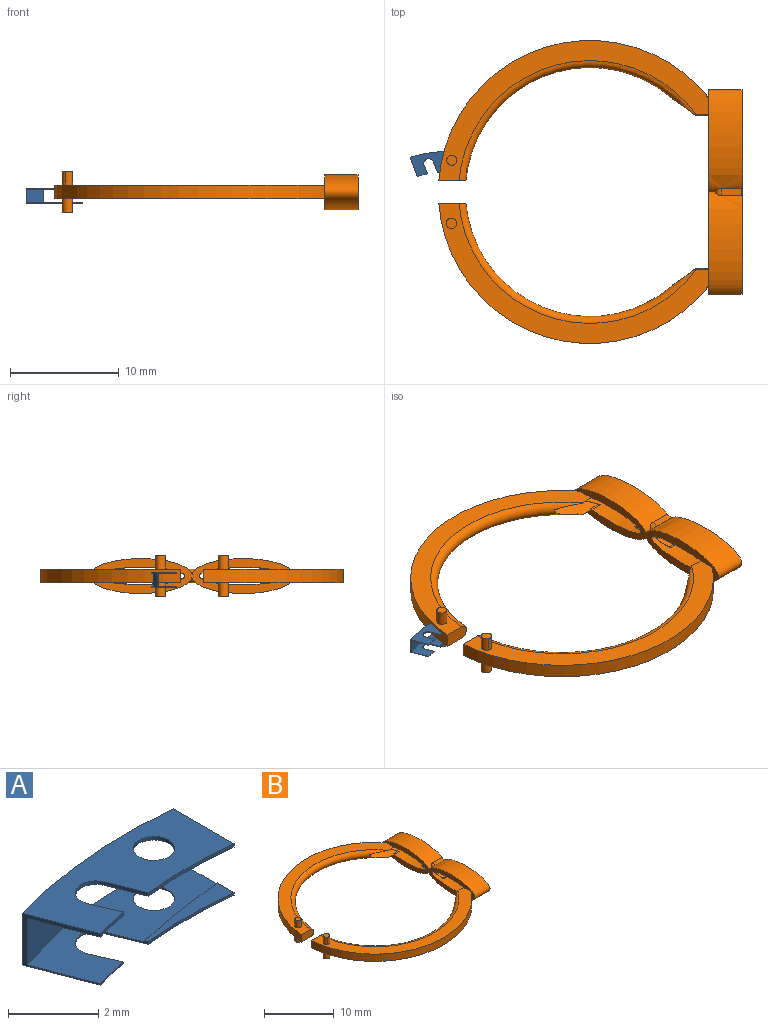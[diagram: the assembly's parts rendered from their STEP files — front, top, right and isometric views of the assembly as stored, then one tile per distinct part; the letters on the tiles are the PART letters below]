
ASSEMBLY  parts=2 mates=1
PART A: 27 faces, bbox 5.2x2.3x1.4 mm
  f0: cylinder r=12.03mm len=0.96mm, axis (0,0,-1), area 0.1mm2, adj f1,f4,f20,f26
  f1: plane 5.2x2.31mm, normal (0,0,1), area 7.4mm2, adj f0,f6,f12,f13,f16,f20,f21,f22
  f2: plane 5.2x2.31mm, normal (0,0,-1), area 7.4mm2, adj f5,f6,f8,f14,f15,f23,f24,f25
  f3: plane 5.15x2.31mm, normal (0,0,1), area 6.5mm2, adj f5,f6,f7,f9,f14,f15,f23,f24
  f4: plane 5.16x2.34mm, normal (0,0,-1), area 6.5mm2, adj f0,f6,f7,f11,f13,f16,f19,f20
  f5: cylinder r=12.03mm len=0.96mm, axis (0,0,-1), area 0mm2, adj f2,f3,f25,f26
  f6: cylinder r=13.92mm len=5.2mm, axis (0,0,-1), area 2.8mm2, adj f1,f2,f3,f4,f7,f13,f14,f17
  f7: cylinder r=23.18mm len=2.05mm, axis (0,0,1), area 2.1mm2, adj f3,f4,f6,f17,f18,f26
  f8: cylinder r=12.03mm len=2.67mm, axis (0,0,-1), area 0.2mm2, adj f2,f10,f14,f24
  f9: cylinder r=21.36mm len=2.7mm, axis (0,0,1), area 0.1mm2, adj f3,f10,f14,f24
  f10: plane 2.7x0.52mm, normal (0,0,1), area 0.8mm2, adj f8,f9,f14,f24
  f11: plane 2.72x0.53mm, normal (0,0,-1), area 0.8mm2, adj f4,f12,f13,f21
  f12: cylinder r=12.03mm len=2.67mm, axis (0,0,-1), area 0.2mm2, adj f1,f11,f13,f21
  f13: plane 1.9x0.09mm, normal (1,0,0), area 0.2mm2, adj f1,f4,f6,f11,f12
  f14: plane 1.9x0.08mm, normal (1,0,0), area 0.1mm2, adj f2,f3,f6,f8,f9,f10
  f15: cylinder r=0.46mm len=0.91mm, axis (0,0,-1), area 0.1mm2, adj f2,f3
  f16: cylinder r=0.46mm len=0.91mm, axis (0,0,-1), area 0.3mm2, adj f1,f4
  f17: plane 0.47x0.11mm, normal (0,0,1), area 0mm2, adj f6,f7,f18
  f18: plane 1.23x0.05mm, normal (1,0,0), area 0.1mm2, adj f6,f7,f17,f19
  f19: plane 0.47x0.12mm, normal (0,0,-1), area 0mm2, adj f4,f6,f18
  f20: plane 0.77x0.33mm, normal (0.92,0.4,0), area 0.1mm2, adj f0,f1,f4,f22
  f21: plane 0.94x0.38mm, normal (-0.93,-0.38,0), area 0.1mm2, adj f1,f4,f11,f12,f22
  f22: cylinder r=0.46mm len=0.9mm, axis (0,0,1), area 0.1mm2, adj f1,f4,f20,f21
  f23: cylinder r=0.46mm len=0.9mm, axis (0,0,1), area 0.1mm2, adj f2,f3,f24,f25
  f24: plane 0.94x0.38mm, normal (-0.93,-0.38,0), area 0mm2, adj f2,f3,f8,f9,f10,f23
  f25: plane 0.77x0.33mm, normal (0.92,0.4,0), area 0mm2, adj f2,f3,f5,f23
  f26: plane 1.77x1.4mm, normal (-0.94,-0.35,0), area 0.4mm2, adj f0,f1,f2,f3,f4,f5,f6,f7
PART B: 52 faces, bbox 28x27.9x3.9 mm
  f0: plane 25.9x12.96mm, normal (0,0,1), area 56.5mm2, adj f2,f4,f16,f27,f39,f42,f45
  f1: cylinder r=13.91mm len=24.8mm, axis (0,0,-1), area 42.4mm2, adj f8,f10,f27,f35,f41
  f2: cylinder r=13.91mm len=24.8mm, axis (0,0,-1), area 42.4mm2, adj f0,f3,f27,f39,f42
  f3: plane 25.89x12.9mm, normal (0,0,-1), area 58.3mm2, adj f2,f4,f6,f15,f27,f39,f42,f50
  f4: torus R=12.07mm, axis (0,0,1), area 53.6mm2, adj f0,f3,f38,f39,f42
  f5: cylinder r=13.91mm len=1.65mm, axis (0,0,-1), area 0mm2, adj f11,f15,f40
  f6: cylinder r=13.91mm len=1.6mm, axis (0,0,-1), area 0.1mm2, adj f3,f15,f39
  f7: cylinder r=13.91mm len=1.6mm, axis (0,0,-1), area 0mm2, adj f10,f21,f35
  f8: plane 25.9x12.96mm, normal (0,0,1), area 56.4mm2, adj f1,f14,f27,f28,f35,f41,f43,f47
  f9: plane 1.9x0.09mm, normal (0,0,1), area 0.1mm2, adj f12,f16,f40
  f10: plane 25.89x12.9mm, normal (0,0,-1), area 58.3mm2, adj f1,f7,f14,f21,f27,f35,f41,f48
  f11: plane 1.9x0.18mm, normal (0,0,-1), area 0.3mm2, adj f5,f13,f15,f40
  f12: torus R=12.07mm, axis (0,0,1), area 0mm2, adj f9,f16,f40
  f13: torus R=12.07mm, axis (0,0,1), area 0.1mm2, adj f11,f15,f40
  f14: torus R=12.07mm, axis (0,0,1), area 53.6mm2, adj f8,f10,f35,f36,f41
  f15: extruded ~7.96x3.05mm, area 20.9mm2, adj f3,f5,f6,f11,f13,f27,f29,f39
  f16: extruded ~7.38x3.05mm, area 19.1mm2, adj f0,f9,f12,f27,f29,f39,f40
  f17: cylinder r=13.91mm len=1.38mm, axis (0,0,-1), area 0mm2, adj f24,f28,f37
  f18: cylinder r=13.91mm len=1.65mm, axis (0,0,-1), area 0mm2, adj f21,f25,f37
  f19: torus R=12.07mm, axis (0,0,1), area 0mm2, adj f24,f28,f37
  f20: torus R=12.07mm, axis (0,0,1), area 0.1mm2, adj f21,f25,f37
  f21: extruded ~7.96x3.05mm, area 20.9mm2, adj f7,f10,f18,f20,f25,f27,f29,f35
  f22: extruded ~9.4x3.22mm, area 60.5mm2, adj f23,f26,f27,f29,f30,f31,f32,f33
  f23: cylinder r=13.91mm len=0.7mm, axis (0,0,-1), area 0.2mm2, adj f22,f32,f34
  f24: plane 1.88x0.07mm, normal (0,0,1), area 0.1mm2, adj f17,f19,f28,f37
  f25: plane 1.9x0.18mm, normal (0,0,-1), area 0.3mm2, adj f18,f20,f21,f37
  f26: torus R=12.07mm, axis (0,0,1), area 0.3mm2, adj f22,f32,f34
  f27: plane 18.88x3.31mm, normal (-1,0,0), area 26.3mm2, adj f0,f1,f2,f3,f8,f10,f15,f16
  f28: extruded ~7.38x3.05mm, area 19.1mm2, adj f8,f17,f19,f24,f27,f29,f35,f37
  f29: plane 18.83x3.26mm, normal (1,0,0), area 27.3mm2, adj f15,f16,f21,f22,f28,f34,f35,f37
  f30: cylinder r=13.91mm len=0.73mm, axis (0,0,-1), area 0.2mm2, adj f22,f31,f34
  f31: plane 1.85x0.73mm, normal (0,0,1), area 1.3mm2, adj f22,f30,f33,f34
  f32: plane 1.85x0.7mm, normal (0,0,-1), area 1.3mm2, adj f22,f23,f26,f34
  f33: torus R=12.07mm, axis (0,0,1), area 0.3mm2, adj f22,f31,f34
  f34: extruded ~9.4x3.22mm, area 60.5mm2, adj f22,f23,f26,f27,f29,f30,f31,f32
  f35: extruded ~7.97x6.35mm, area 12.2mm2, adj f1,f7,f8,f10,f14,f21,f27,f28
  f36: plane 0.37x0.15mm, normal (1,0,0), area 0mm2, adj f14,f35
  f37: extruded ~3.05x1.65mm, area 8.4mm2, adj f17,f18,f19,f20,f21,f24,f25,f27
  f38: plane 0.37x0.15mm, normal (1,0,0), area 0mm2, adj f4,f39
  f39: extruded ~7.97x6.35mm, area 12.2mm2, adj f0,f2,f3,f4,f6,f15,f16,f27
  f40: extruded ~3.05x1.65mm, area 8.4mm2, adj f5,f9,f11,f12,f13,f15,f16,f27
  f41: plane 2.59x1.38mm, normal (0,1,0), area 3mm2, adj f1,f8,f10,f14
  f42: plane 2.59x1.38mm, normal (0,-1,0), area 3mm2, adj f0,f2,f3,f4
  f43: cylinder r=0.46mm len=1.27mm, axis (0,0,-1), area 1.5mm2, adj f8,f44,f47
  f44: plane 0.95x0.95mm, normal (0,0,1), area 0.7mm2, adj f43,f47
  f45: cylinder r=0.46mm len=1.27mm, axis (0,0,-1), area 3.6mm2, adj f0,f46
  f46: plane 0.91x0.91mm, normal (0,0,1), area 0.7mm2, adj f45
  f47: cylinder r=0.47mm len=1.27mm, axis (0,0,1), area 2.3mm2, adj f8,f43,f44
  f48: cylinder r=0.47mm len=1.27mm, axis (0,0,1), area 3.8mm2, adj f10,f49
  f49: plane 0.94x0.94mm, normal (0,0,-1), area 0.7mm2, adj f48
  f50: cylinder r=0.46mm len=1.27mm, axis (0,0,1), area 3.6mm2, adj f3,f51
  f51: plane 0.91x0.91mm, normal (0,0,-1), area 0.7mm2, adj f50
PLACE A t=(-18.64,-5.66,9.12)mm
PLACE B t=(-5.94,-8.56,9.53)mm
MATE slider B.f45 <-> A.f15  axis (0,0,1) through (-18.64,-5.66,12.07)mm
